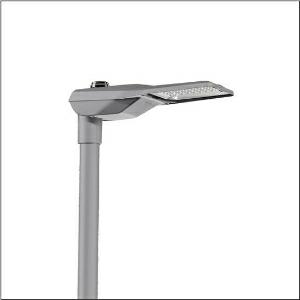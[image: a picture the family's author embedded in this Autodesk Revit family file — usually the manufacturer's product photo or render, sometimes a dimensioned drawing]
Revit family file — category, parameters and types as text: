
# Revit family: streetlight_sl_21_mini___st0_8a_5xe6c37n08hb_0120
name_source: partatom
category: Lighting Fixtures
units: mm (PartAtom-declared; Revit-internal decimal feet)

## family parameters
Cut with Voids When Loaded = No
Host = Face
Light Source = No
Part Type = Normal
Room Calculation Point = No
Round Connector Dimension = Use Diameter
Shared = No

## types (1)
- --- (1 x LED, 9040 lm, 66 W, 3000K)
    Apparent Load = 66 VA
    CIE Flux Codes = 38 75 97 100 100
    Color Rendering = 70
    Color Temperature = 3000K
    Default Elevation = 1800 mm
    Description = Streetlight SL 21 mini, mast luminaire, primary light control with lens, of PMMA, primary optical cover: cover, of toughened safety glass, transparent, light distribution: ST0.8a, light emission: direct distribution, primary light characteristic: asymmetric, installation type: side-entry, LED, 3G 1.5mm², High Power LED, rated luminous flux: 9.040lm, luminous efficacy: 137lm/W, light colour: 730, colour temperature: 3000K, control gear: NEMA (7pin), control: overheat protection, pre-setting: linear dimming characteristic, constant luminous flux control, time-dependent luminous flux control, flexible luminous flux parameterisation, mains connection: 230..240V, AC, 50/60Hz, connection cable pre-assembled, cable length: 8,5m, wiring characteristics: H07RN-F, start of lifetime: 66W, end of service life: 69W, reduction: 30W, luminaire housing, of diecast aluminium (EN AC-44300), powder-coated, Siteco® metallic grey (DB 702S), corrosivity category C5 mid according to DIN EN ISO 12944, multi-level sealing system, sealing non-destructively replaceable, inclination adjustable: 0°, 5°, 10°, 15°, length: 628mm, width: 235mm, height: 110mm, spigot size: 42mm (side-entry), mounting height: 4..8m, protection rating (complete): IP66, insulation class (complete): insulation class I (protective earthing), certification: CE, ENEC, ENEC+, VDE, impact resistance: IK10, permissible operating ambient temperature for outdoor applications: -40..+50°C, standard-compliant lighting for roads and squares, packaging unit: 1 piece

Light Distribution: ST0.8a
    Height = 110 mm
    Lamp = 1 x LED
    Lamp Light Flux = 9040 lm
    Lamp Power = 66 W
    Lamp count = 1
    Length = 625 mm
    Luminous efficacy = 137 lm/W
    Manufacturer = Siteco
    ModVariant = No
    Model = 5XE6C37N08HB
    Number of Poles = 1
    OnlyDefault = Yes
    Power Factor = 1
    Product Name = Streetlight SL 21 mini | ST0.8a
    Product group = mast luminaire | pylon top
    ProductGroupID = 6100
    Protection Class = Protection class I
    Protection Degree = IP 66
    RLX_Detail_Level = 1
    RLX_Emergency_Light_Flux = 0 lm
    RLX_Emergency_Type = 0
    RLX_Emergency_Type_DB = No
    RlxData = <blob elided: 26209 chars, md5=9c552098>
    Socket = socket
    Standby Power = 0 W
    System Light Flux = 9040 lm
    System Power = 66 W
    Type Comments = factory setting: luminous flux: 100 % | dim-lin: 254 | 670 mA
    Type Image = l_1294379.jpg
    URL = http://relux.com
    VarID = @adj_155705
    Voltage = 0 V
    Weight = 0.00 kg
    Width = 234 mm

## geometry (parser evidence)
native form markers: Blend x4, Sweep x9
no freeform markers — native parametric forms only
